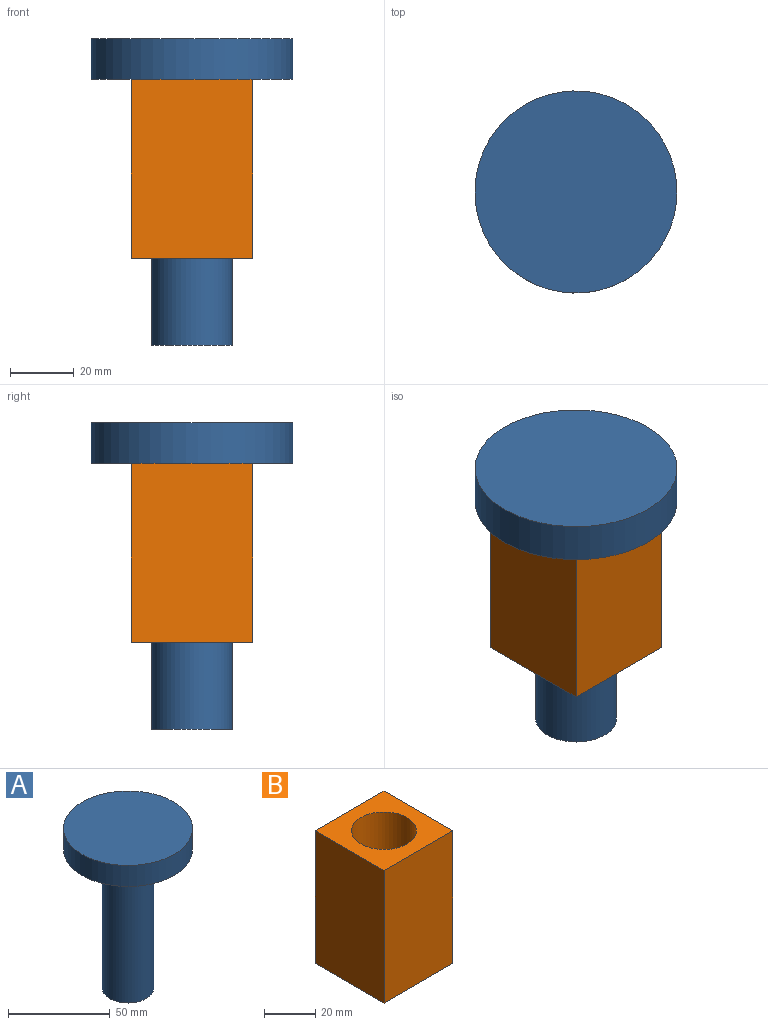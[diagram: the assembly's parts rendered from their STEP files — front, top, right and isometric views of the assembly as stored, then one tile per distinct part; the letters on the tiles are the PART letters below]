
ASSEMBLY  parts=2 mates=1
PART A: 5 faces, bbox 63.5x63.5x96.4 mm
  f0: cylinder r=31.75mm len=63.5mm, axis (0,0,1), area 2533.5mm2, adj f1,f2
  f1: plane 63.5x63.5mm, normal (0,0,-1), area 2660.2mm2, adj f0,f3
  f2: plane 63.5x63.5mm, normal (0,0,1), area 3166.9mm2, adj f0
  f3: cylinder r=12.7mm len=83.66mm, axis (0,0,1), area 6675.5mm2, adj f1,f4
  f4: plane 25.4x25.4mm, normal (0,0,-1), area 506.7mm2, adj f3
PART B: 7 faces, bbox 38.1x38.1x63.5 mm
  f0: plane 63.5x38.1mm, normal (-1,0,0), area 2419.4mm2, adj f1,f4,f5,f6
  f1: plane 63.5x38.1mm, normal (0,-1,0), area 2419.4mm2, adj f0,f2,f5,f6
  f2: plane 63.5x38.1mm, normal (1,0,0), area 2419.3mm2, adj f1,f4,f5,f6
  f3: cylinder r=12.7mm len=63.5mm, axis (0,0,-1), area 5067.1mm2, adj f5,f6
  f4: plane 63.5x38.1mm, normal (0,1,0), area 2419.4mm2, adj f0,f2,f5,f6
  f5: plane 38.1x38.1mm, normal (0,0,1), area 944.9mm2, adj f0,f1,f2,f3,f4
  f6: plane 38.1x38.1mm, normal (0,0,-1), area 944.9mm2, adj f0,f1,f2,f3,f4
PLACE A t=(15.46,14.14,66.51)mm
PLACE B t=(-3.59,-4.91,-2.42)mm
MATE slider A.f3 <-> B.f3  axis (0,0,1) through (15.46,14.14,-29.85)mm
